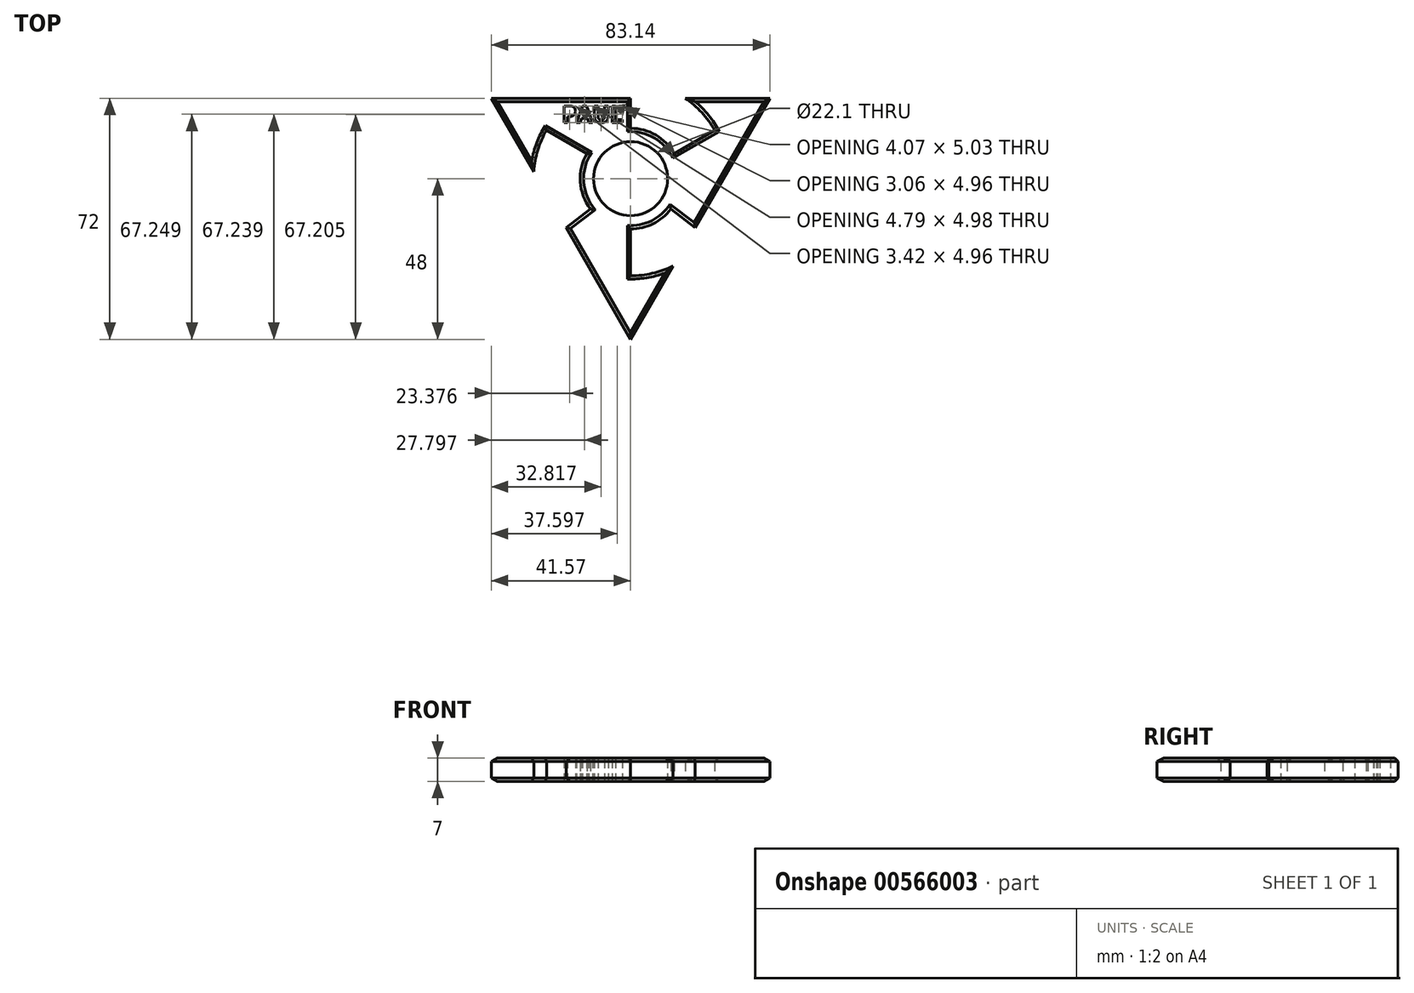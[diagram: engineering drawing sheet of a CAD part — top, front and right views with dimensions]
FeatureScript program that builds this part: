
annotation { "Feature Type Name" : "Feature", "Feature Type Description" : "" }
export const myFeature = defineFeature(function(context is Context, id is Id, definition is map)
    precondition{}
    {
        {
            var Q0;
            Q0=qCreatedBy(makeId("Top.planeOp"),FACE);
            var sketch = newSketch(context, id + "F0", { "sketchPlane" : qUnion([Q0])});
            skCircle(sketch, "E0", {"center": v(0, 0) * mm, "radius": 11.05 * mm});
            skLineSegment(sketch, "E1", {"start": v(41.57, 24) * mm, "end": v(19.28, -14.61) * mm});
            skLineSegment(sketch, "E2", {"start": v(0, -48) * mm, "end": v(-19.28, -14.61) * mm});
            skLineSegment(sketch, "E3", {"start": v(0, 24) * mm, "end": v(-41.57, 24) * mm});
            skLineSegment(sketch, "E4", {"start": v(9.57, 5.53) * mm, "end": v(25.11, 14.5) * mm});
            skLineSegment(sketch, "E5", {"start": v(-9.57, 5.52) * mm, "end": v(-25.11, 14.5) * mm});
            skLineSegment(sketch, "E6", {"start": v(0, -11.05) * mm, "end": v(0, -29) * mm});
            skArc(sketch, "E7", {"start": v(-25.11, 14.5) * mm, "mid": v(-27.72, 8.51) * mm, "end": v(-28.92, 2.1) * mm});
            skLineSegment(sketch, "E8", {"start": v(-19.28, -14.61) * mm, "end": v(-8.8, -6.68) * mm});
            skLineSegment(sketch, "E9", {"start": v(19.28, -14.61) * mm, "end": v(8.8, -6.68) * mm});
            skLineSegment(sketch, "E10", {"start": v(0, 24) * mm, "end": v(0, 11.05) * mm});
            skLineSegment(sketch, "E11.trimOffspring", {"start": v(-28.92, 2.1) * mm, "end": v(-41.57, 24) * mm});
            skArc(sketch, "E12.trimOffspring", {"start": v(0, -29) * mm, "mid": v(6.49, -28.27) * mm, "end": v(12.65, -26.1) * mm});
            skLineSegment(sketch, "E13.trimOffspring", {"start": v(16.28, 24) * mm, "end": v(41.57, 24) * mm});
            skArc(sketch, "E14.trimOffspring", {"start": v(25.11, 14.5) * mm, "mid": v(21.23, 19.75) * mm, "end": v(16.28, 24) * mm});
            skLineSegment(sketch, "E15.trimOffspring", {"start": v(12.65, -26.1) * mm, "end": v(0, -48) * mm});
            skCircle(sketch, "E16", {"center": v(0, 0) * mm, "radius": 15.04 * mm});
            skText(sketch, "E17", { "text": "PAUL", "fontName": "OpenSans-Bold.ttf"});
            const initialGuessF0  = {"E17": [-0.02053, 0.01676, 1, 0, 0.005]};
            skSetInitialGuess(sketch, initialGuessF0);
            skSolve(sketch);
        }
        {
            var Q0;
            Q0 = qSketchRegion(id + "F0", true);
            extrude(context, id + "F1", {"entities" : qUnion([Q0]), "depth" : 7 * mm, "offsetDistance" : 25 * mm});
        }
        {
            var Q0;
            Q0=makeQuery(id+"F1.opExtrude","CAP_EDGE",EDGE,{"disambiguationData":[OSD([sQuery(id+"F0.wireOp",EDGE,"E3")])],"isStart":false});
            var Q1;
            Q1=makeQuery(id+"F1.opExtrude","CAP_EDGE",EDGE,{"disambiguationData":[OSD([sQuery(id+"F0.wireOp",EDGE,"E11.trimOffspring")])],"isStart":false});
            var Q2;
            Q2=makeQuery(id+"F1.opExtrude","CAP_EDGE",EDGE,{"disambiguationData":[OSD([sQuery(id+"F0.wireOp",EDGE,"E5")])],"isStart":false});
            var Q3;
            {var subQ0=sQuery(id+"F0.wireOp",EDGE,"E16");Q3=makeQuery(id+"F1.opExtrude","CAP_EDGE",EDGE,{"disambiguationData":[OSD([subQ0]),TDD([makeQuery(id+"F0.imprint","IMPRINT",EDGE,{"disambiguationData":[TD([[makeQuery(id+"F0.imprint","INTERSECT",VERTEX,{"derivedFrom":[sQuery(id+"F0.wireOp",EDGE,"E5"),subQ0]}),-1.0]])],"derivedFrom":subQ0})])],"isStart":false});}
            var Q4;
            Q4=makeQuery(id+"F1.opExtrude","CAP_EDGE",EDGE,{"disambiguationData":[OSD([sQuery(id+"F0.wireOp",EDGE,"E7")])],"isStart":false});
            var Q5;
            Q5=makeQuery(id+"F1.opExtrude","CAP_EDGE",EDGE,{"disambiguationData":[OSD([sQuery(id+"F0.wireOp",EDGE,"E8")])],"isStart":false});
            var Q6;
            Q6=makeQuery(id+"F1.opExtrude","CAP_EDGE",EDGE,{"disambiguationData":[OSD([sQuery(id+"F0.wireOp",EDGE,"E2")])],"isStart":false});
            var Q7;
            Q7=makeQuery(id+"F1.opExtrude","CAP_EDGE",EDGE,{"disambiguationData":[OSD([sQuery(id+"F0.wireOp",EDGE,"E15.trimOffspring")])],"isStart":false});
            var Q8;
            {var subQ0=sQuery(id+"F0.wireOp",EDGE,"E16");Q8=makeQuery(id+"F1.opExtrude","CAP_EDGE",EDGE,{"disambiguationData":[OSD([subQ0]),TDD([makeQuery(id+"F0.imprint","IMPRINT",EDGE,{"disambiguationData":[TD([[makeQuery(id+"F0.imprint","INTERSECT",VERTEX,{"derivedFrom":[sQuery(id+"F0.wireOp",EDGE,"E6"),subQ0]}),-1.0]])],"derivedFrom":subQ0})])],"isStart":false});}
            var Q9;
            Q9=makeQuery(id+"F1.opExtrude","CAP_EDGE",EDGE,{"disambiguationData":[OSD([sQuery(id+"F0.wireOp",EDGE,"E6")])],"isStart":false});
            var Q10;
            Q10=makeQuery(id+"F1.opExtrude","CAP_EDGE",EDGE,{"disambiguationData":[OSD([sQuery(id+"F0.wireOp",EDGE,"E12.trimOffspring")])],"isStart":false});
            var Q11;
            Q11=makeQuery(id+"F1.opExtrude","CAP_EDGE",EDGE,{"disambiguationData":[OSD([sQuery(id+"F0.wireOp",EDGE,"E9")])],"isStart":false});
            var Q12;
            Q12=makeQuery(id+"F1.opExtrude","CAP_EDGE",EDGE,{"disambiguationData":[OSD([sQuery(id+"F0.wireOp",EDGE,"E1")])],"isStart":false});
            var Q13;
            Q13=makeQuery(id+"F1.opExtrude","CAP_EDGE",EDGE,{"disambiguationData":[OSD([sQuery(id+"F0.wireOp",EDGE,"E13.trimOffspring")])],"isStart":false});
            var Q14;
            Q14=makeQuery(id+"F1.opExtrude","CAP_EDGE",EDGE,{"disambiguationData":[OSD([sQuery(id+"F0.wireOp",EDGE,"E14.trimOffspring")])],"isStart":false});
            var Q15;
            Q15=makeQuery(id+"F1.opExtrude","CAP_EDGE",EDGE,{"disambiguationData":[OSD([sQuery(id+"F0.wireOp",EDGE,"E4")])],"isStart":false});
            var Q16;
            {var subQ0=sQuery(id+"F0.wireOp",EDGE,"E16");Q16=makeQuery(id+"F1.opExtrude","CAP_EDGE",EDGE,{"disambiguationData":[OSD([subQ0]),TDD([makeQuery(id+"F0.imprint","IMPRINT",EDGE,{"disambiguationData":[TD([[makeQuery(id+"F0.imprint","INTERSECT",VERTEX,{"derivedFrom":[sQuery(id+"F0.wireOp",EDGE,"E4"),subQ0]}),-1.0]])],"derivedFrom":subQ0})])],"isStart":false});}
            var Q17;
            Q17=makeQuery(id+"F1.opExtrude","CAP_EDGE",EDGE,{"disambiguationData":[OSD([sQuery(id+"F0.wireOp",EDGE,"E10")])],"isStart":false});
            chamfer(context, id + "F2", {"entities" : qUnion([Q0, Q1, Q2, Q3, Q4, Q5, Q6, Q7, Q8, Q9, Q10, Q11, Q12, Q13, Q14, Q15, Q16, Q17]), "width" : 1 * mm, "tangentPropagation" : true});
        }
        {
            var Q0;
            Q0=makeQuery(id+"F1.opExtrude","CAP_EDGE",EDGE,{"disambiguationData":[OSD([sQuery(id+"F0.wireOp",EDGE,"E2")])],"isStart":true});
            var Q1;
            Q1=makeQuery(id+"F1.opExtrude","CAP_EDGE",EDGE,{"disambiguationData":[OSD([sQuery(id+"F0.wireOp",EDGE,"E15.trimOffspring")])],"isStart":true});
            var Q2;
            Q2=makeQuery(id+"F1.opExtrude","CAP_EDGE",EDGE,{"disambiguationData":[OSD([sQuery(id+"F0.wireOp",EDGE,"E6")])],"isStart":true});
            var Q3;
            Q3=makeQuery(id+"F1.opExtrude","CAP_EDGE",EDGE,{"disambiguationData":[OSD([sQuery(id+"F0.wireOp",EDGE,"E12.trimOffspring")])],"isStart":true});
            var Q4;
            {var subQ0=sQuery(id+"F0.wireOp",EDGE,"E16");Q4=makeQuery(id+"F1.opExtrude","CAP_EDGE",EDGE,{"disambiguationData":[OSD([subQ0]),TDD([makeQuery(id+"F0.imprint","IMPRINT",EDGE,{"disambiguationData":[TD([[makeQuery(id+"F0.imprint","INTERSECT",VERTEX,{"derivedFrom":[sQuery(id+"F0.wireOp",EDGE,"E6"),subQ0]}),-1.0]])],"derivedFrom":subQ0})])],"isStart":true});}
            var Q5;
            Q5=makeQuery(id+"F1.opExtrude","CAP_EDGE",EDGE,{"disambiguationData":[OSD([sQuery(id+"F0.wireOp",EDGE,"E9")])],"isStart":true});
            var Q6;
            Q6=makeQuery(id+"F1.opExtrude","CAP_EDGE",EDGE,{"disambiguationData":[OSD([sQuery(id+"F0.wireOp",EDGE,"E1")])],"isStart":true});
            var Q7;
            Q7=makeQuery(id+"F1.opExtrude","CAP_EDGE",EDGE,{"disambiguationData":[OSD([sQuery(id+"F0.wireOp",EDGE,"E13.trimOffspring")])],"isStart":true});
            var Q8;
            Q8=makeQuery(id+"F1.opExtrude","CAP_EDGE",EDGE,{"disambiguationData":[OSD([sQuery(id+"F0.wireOp",EDGE,"E14.trimOffspring")])],"isStart":true});
            var Q9;
            Q9=makeQuery(id+"F1.opExtrude","CAP_EDGE",EDGE,{"disambiguationData":[OSD([sQuery(id+"F0.wireOp",EDGE,"E4")])],"isStart":true});
            var Q10;
            {var subQ0=sQuery(id+"F0.wireOp",EDGE,"E16");Q10=makeQuery(id+"F1.opExtrude","CAP_EDGE",EDGE,{"disambiguationData":[OSD([subQ0]),TDD([makeQuery(id+"F0.imprint","IMPRINT",EDGE,{"disambiguationData":[TD([[makeQuery(id+"F0.imprint","INTERSECT",VERTEX,{"derivedFrom":[sQuery(id+"F0.wireOp",EDGE,"E4"),subQ0]}),-1.0]])],"derivedFrom":subQ0})])],"isStart":true});}
            var Q11;
            Q11=makeQuery(id+"F1.opExtrude","CAP_EDGE",EDGE,{"disambiguationData":[OSD([sQuery(id+"F0.wireOp",EDGE,"E10")])],"isStart":true});
            var Q12;
            Q12=makeQuery(id+"F1.opExtrude","CAP_EDGE",EDGE,{"disambiguationData":[OSD([sQuery(id+"F0.wireOp",EDGE,"E3")])],"isStart":true});
            var Q13;
            Q13=makeQuery(id+"F1.opExtrude","CAP_EDGE",EDGE,{"disambiguationData":[OSD([sQuery(id+"F0.wireOp",EDGE,"E11.trimOffspring")])],"isStart":true});
            var Q14;
            Q14=makeQuery(id+"F1.opExtrude","CAP_EDGE",EDGE,{"disambiguationData":[OSD([sQuery(id+"F0.wireOp",EDGE,"E7")])],"isStart":true});
            var Q15;
            Q15=makeQuery(id+"F1.opExtrude","CAP_EDGE",EDGE,{"disambiguationData":[OSD([sQuery(id+"F0.wireOp",EDGE,"E5")])],"isStart":true});
            var Q16;
            {var subQ0=sQuery(id+"F0.wireOp",EDGE,"E16");Q16=makeQuery(id+"F1.opExtrude","CAP_EDGE",EDGE,{"disambiguationData":[OSD([subQ0]),TDD([makeQuery(id+"F0.imprint","IMPRINT",EDGE,{"disambiguationData":[TD([[makeQuery(id+"F0.imprint","INTERSECT",VERTEX,{"derivedFrom":[sQuery(id+"F0.wireOp",EDGE,"E5"),subQ0]}),-1.0]])],"derivedFrom":subQ0})])],"isStart":true});}
            var Q17;
            Q17=makeQuery(id+"F1.opExtrude","CAP_EDGE",EDGE,{"disambiguationData":[OSD([sQuery(id+"F0.wireOp",EDGE,"E8")])],"isStart":true});
            chamfer(context, id + "F3", {"entities" : qUnion([Q0, Q1, Q2, Q3, Q4, Q5, Q6, Q7, Q8, Q9, Q10, Q11, Q12, Q13, Q14, Q15, Q16, Q17]), "width" : 1 * mm, "tangentPropagation" : true});
        }
    });
